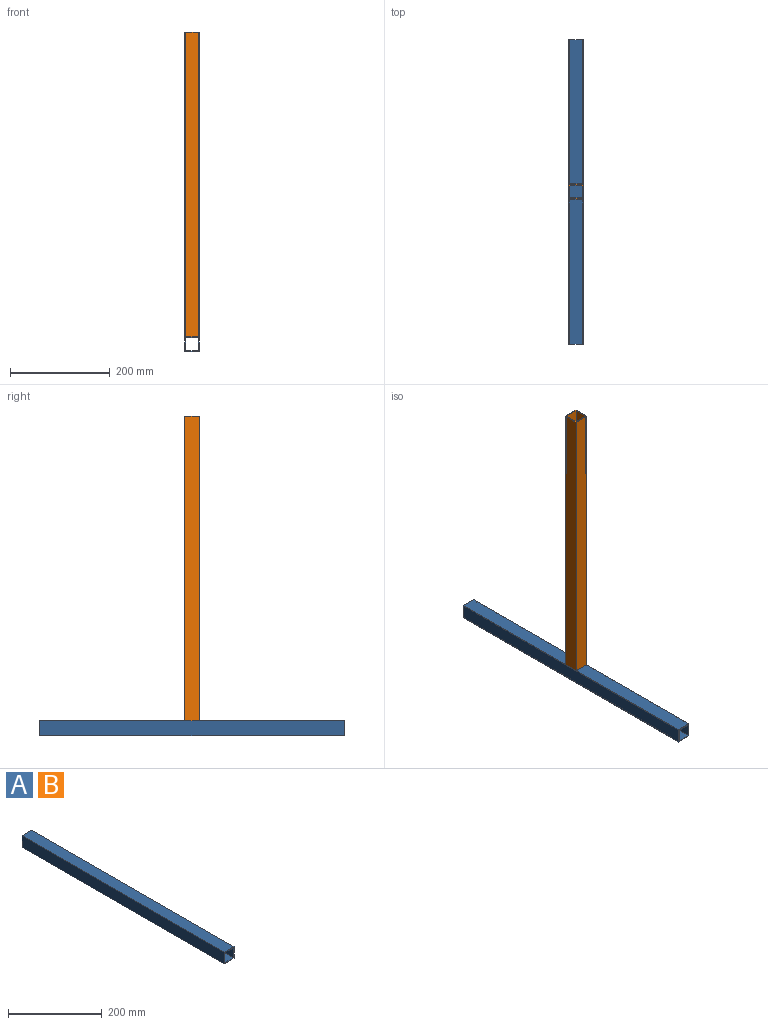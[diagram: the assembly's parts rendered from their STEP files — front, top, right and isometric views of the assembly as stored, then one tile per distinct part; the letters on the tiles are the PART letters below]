
ASSEMBLY  parts=2 mates=1
PART A: 10 faces, bbox 30x609.6x30 mm
  f0: plane 609.6x26mm, normal (-1,0,0), area 15849.6mm2, adj f1,f7,f8,f9
  f1: plane 609.6x26mm, normal (0,0,1), area 15849.6mm2, adj f0,f2,f8,f9
  f2: plane 609.6x26mm, normal (1,0,0), area 15849.6mm2, adj f1,f7,f8,f9
  f3: plane 609.6x30mm, normal (0,0,-1), area 18288mm2, adj f4,f6,f8,f9
  f4: plane 609.6x30mm, normal (1,0,0), area 18288mm2, adj f3,f5,f8,f9
  f5: plane 609.6x30mm, normal (0,0,1), area 18288mm2, adj f4,f6,f8,f9
  f6: plane 609.6x30mm, normal (-1,0,0), area 18288mm2, adj f3,f5,f8,f9
  f7: plane 609.6x26mm, normal (0,0,-1), area 15849.6mm2, adj f0,f2,f8,f9
  f8: plane 30x30mm, normal (0,-1,0), area 224mm2, adj f0,f1,f2,f3,f4,f5,f6,f7
  f9: plane 30x30mm, normal (0,1,0), area 224mm2, adj f0,f1,f2,f3,f4,f5,f6,f7
PART B: same geometry as A
PLACE A t=(-26.86,-12.1,5.11)mm fixed
PLACE B rot(axis=(1,0,0),90deg) t=(-26.86,-12.1,324.91)mm
MATE fastened B.f4 <-> A.f4  axis (1,0,0) through (-11.86,-12.1,20.11)mm
